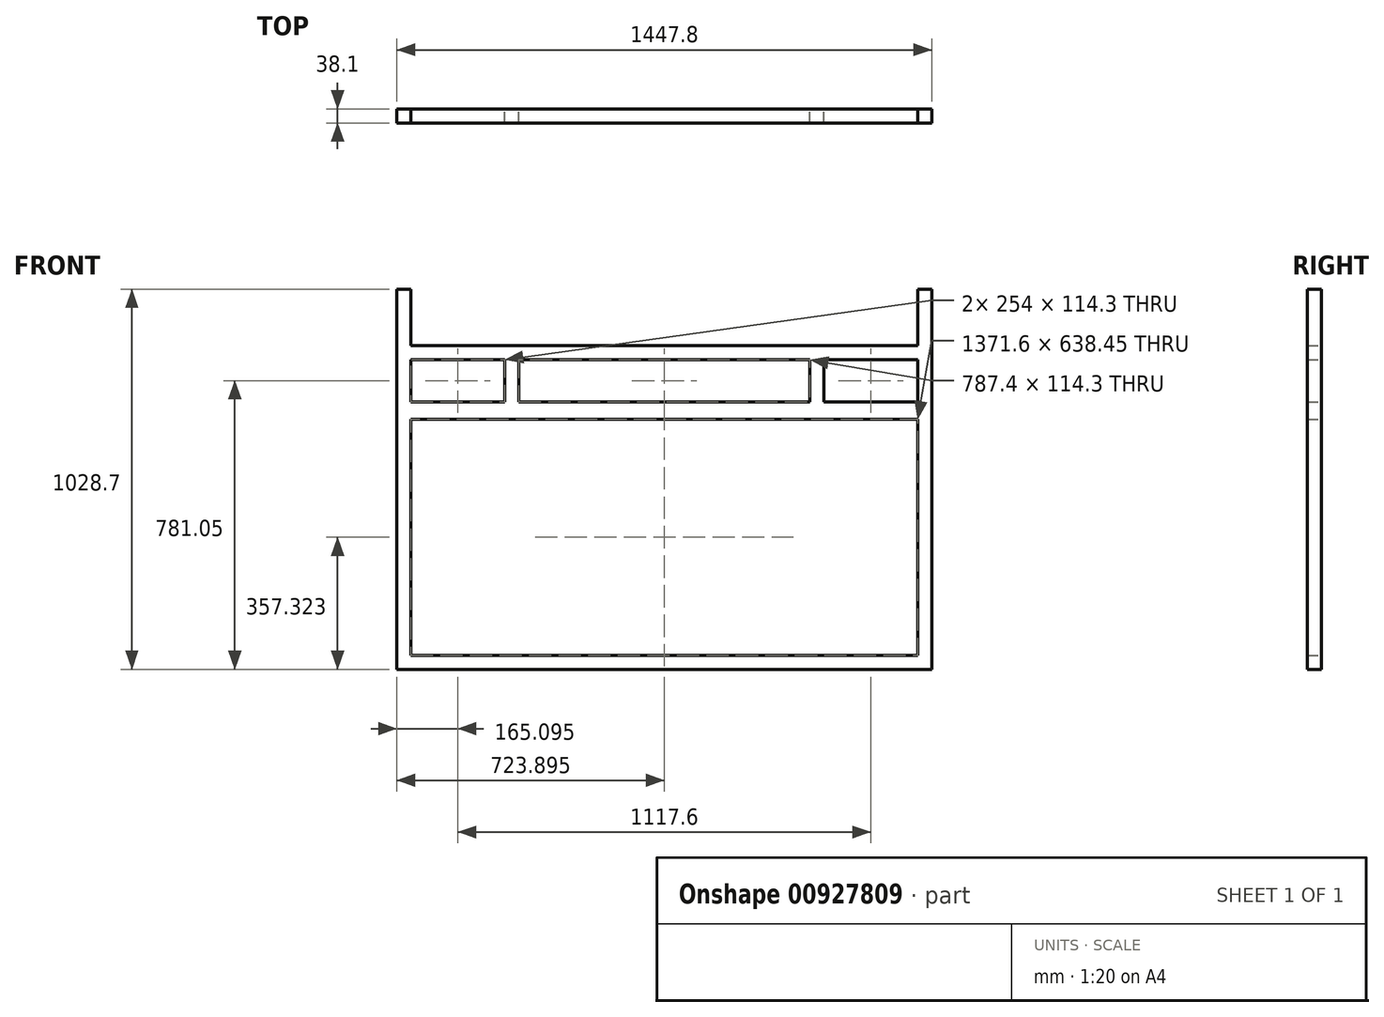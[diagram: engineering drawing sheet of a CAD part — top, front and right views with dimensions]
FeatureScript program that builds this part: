
annotation { "Feature Type Name" : "Feature", "Feature Type Description" : "" }
export const myFeature = defineFeature(function(context is Context, id is Id, definition is map)
    precondition{}
    {
        {
            var Q0;
            Q0=qCreatedBy(makeId("Front.planeOp"),FACE);
            var sketch = newSketch(context, id + "F0", { "sketchPlane" : qUnion([Q0])});
            skLineSegment(sketch, "E0.bottom", {"start": v(-457.01, 0) * mm, "end": v(990.79, 0) * mm});
            skLineSegment(sketch, "E0.top", {"start": v(-457.01, 38.1) * mm, "end": v(990.79, 38.1) * mm});
            skLineSegment(sketch, "E0.left", {"start": v(-457.01, 0) * mm, "end": v(-457.01, 38.1) * mm});
            skLineSegment(sketch, "E0.right", {"start": v(990.79, 0) * mm, "end": v(990.79, 38.1) * mm});
            skLineSegment(sketch, "E1", {"start": v(-457.01, 38.1) * mm, "end": v(-457.01, 723.9) * mm});
            skLineSegment(sketch, "E2.bottom", {"start": v(-457.01, 38.1) * mm, "end": v(-418.91, 38.1) * mm});
            skLineSegment(sketch, "E2.top", {"start": v(-457.01, 723.9) * mm, "end": v(-418.91, 723.9) * mm});
            skLineSegment(sketch, "E2.right", {"start": v(-418.91, 38.1) * mm, "end": v(-418.91, 723.9) * mm});
            skLineSegment(sketch, "E3.bottom", {"start": v(990.79, 38.1) * mm, "end": v(952.69, 38.1) * mm});
            skLineSegment(sketch, "E3.top", {"start": v(990.79, 723.9) * mm, "end": v(952.69, 723.9) * mm});
            skLineSegment(sketch, "E3.left", {"start": v(990.79, 38.1) * mm, "end": v(990.79, 723.9) * mm});
            skLineSegment(sketch, "E3.right", {"start": v(952.69, 38.1) * mm, "end": v(952.69, 723.9) * mm});
            skLineSegment(sketch, "E4.bottom", {"start": v(-418.91, 723.9) * mm, "end": v(952.69, 723.9) * mm});
            skLineSegment(sketch, "E4.top", {"start": v(-418.91, 676.55) * mm, "end": v(952.69, 676.55) * mm});
            skLineSegment(sketch, "E4.left", {"start": v(-418.91, 723.9) * mm, "end": v(-418.91, 676.55) * mm});
            skLineSegment(sketch, "E4.right", {"start": v(952.69, 723.9) * mm, "end": v(952.69, 676.55) * mm});
            skLineSegment(sketch, "E5.top", {"start": v(-457.01, 1028.7) * mm, "end": v(-418.91, 1028.7) * mm});
            skLineSegment(sketch, "E5.left", {"start": v(-457.01, 723.9) * mm, "end": v(-457.01, 1028.7) * mm});
            skLineSegment(sketch, "E5.right", {"start": v(-418.91, 723.9) * mm, "end": v(-418.91, 1028.7) * mm});
            skLineSegment(sketch, "E6.top", {"start": v(990.79, 1028.7) * mm, "end": v(952.69, 1028.7) * mm});
            skLineSegment(sketch, "E6.left", {"start": v(990.79, 723.9) * mm, "end": v(990.79, 1028.7) * mm});
            skLineSegment(sketch, "E6.right", {"start": v(952.69, 723.9) * mm, "end": v(952.69, 1028.7) * mm});
            skLineSegment(sketch, "E7.bottom", {"start": v(-418.91, 876.3) * mm, "end": v(952.69, 876.3) * mm});
            skLineSegment(sketch, "E7.top", {"start": v(-418.91, 838.2) * mm, "end": v(952.69, 838.2) * mm});
            skLineSegment(sketch, "E7.left", {"start": v(-418.91, 876.3) * mm, "end": v(-418.91, 838.2) * mm});
            skLineSegment(sketch, "E7.right", {"start": v(952.69, 876.3) * mm, "end": v(952.69, 838.2) * mm});
            skLineSegment(sketch, "E8.bottom", {"start": v(-164.91, 838.2) * mm, "end": v(-126.81, 838.2) * mm});
            skLineSegment(sketch, "E8.top", {"start": v(-164.91, 723.9) * mm, "end": v(-126.81, 723.9) * mm});
            skLineSegment(sketch, "E8.left", {"start": v(-164.91, 838.2) * mm, "end": v(-164.91, 723.9) * mm});
            skLineSegment(sketch, "E8.right", {"start": v(-126.81, 838.2) * mm, "end": v(-126.81, 723.9) * mm});
            skLineSegment(sketch, "E9.bottom", {"start": v(660.59, 838.2) * mm, "end": v(698.69, 838.2) * mm});
            skLineSegment(sketch, "E9.top", {"start": v(660.59, 723.9) * mm, "end": v(698.69, 723.9) * mm});
            skLineSegment(sketch, "E9.left", {"start": v(660.59, 838.2) * mm, "end": v(660.59, 723.9) * mm});
            skLineSegment(sketch, "E9.right", {"start": v(698.69, 838.2) * mm, "end": v(698.69, 723.9) * mm});
            skSolve(sketch);
        }
        {
            var Q0;
            {var subQ2=sQuery(id+"F0.wireOp",EDGE,"E7.bottom");var subQ4=sQuery(id+"F0.wireOp",EDGE,"E3.top");var subQ5=makeQuery(id+"F0.imprint","IMPRINT",EDGE,{"derivedFrom":subQ4});var subQ12=sQuery(id+"F0.wireOp",EDGE,"E2.top");var subQ13=makeQuery(id+"F0.imprint","IMPRINT",EDGE,{"derivedFrom":subQ12});var subQ14=sQuery(id+"F0.wireOp",EDGE,"E1");Q0=qUnion([makeQuery(id+"F0.imprint","IMPRINT",FACE,{"disambiguationData":[TD([[makeQuery(id+"F0.imprint","IMPRINT",EDGE,{"derivedFrom":sQuery(id+"F0.wireOp",EDGE,"E0.bottom")}),1.0]])]}),makeQuery(id+"F0.imprint","IMPRINT",FACE,{"disambiguationData":[TD([[subQ5,1.0]])]}),makeQuery(id+"F0.imprint","IMPRINT",FACE,{"disambiguationData":[TD([[makeQuery(id+"F0.imprint","IMPRINT",EDGE,{"derivedFrom":subQ2}),-1.0]])]}),makeQuery(id+"F0.imprint","IMPRINT",FACE,{"disambiguationData":[TD([[subQ13,1.0]])]}),makeQuery(id+"F0.imprint","IMPRINT",FACE,{"disambiguationData":[TD([[makeQuery(id+"F0.imprint","IMPRINT",EDGE,{"derivedFrom":subQ14}),-1.0]])]}),makeQuery(id+"F0.imprint","IMPRINT",FACE,{"disambiguationData":[TD([[subQ5,-1.0]])]})]);}
            var Q1;
            {var subQ2=sQuery(id+"F0.wireOp",EDGE,"E8.left");Q1=makeQuery(id+"F0.imprint","IMPRINT",FACE,{"disambiguationData":[TD([[makeQuery(id+"F0.imprint","IMPRINT",EDGE,{"derivedFrom":subQ2}),1.0]])]});}
            var Q2;
            {var subQ4=sQuery(id+"F0.wireOp",EDGE,"E4.top");Q2=makeQuery(id+"F0.imprint","IMPRINT",FACE,{"disambiguationData":[TD([[makeQuery(id+"F0.imprint","IMPRINT",EDGE,{"derivedFrom":subQ4}),1.0]])]});}
            var Q3;
            {var subQ0=sQuery(id+"F0.wireOp",EDGE,"E9.left");Q3=makeQuery(id+"F0.imprint","IMPRINT",FACE,{"disambiguationData":[TD([[makeQuery(id+"F0.imprint","IMPRINT",EDGE,{"derivedFrom":subQ0}),1.0]])]});}
            extrude(context, id + "F1", {"entities" : qUnion([Q0, Q1, Q2, Q3]), "depth" : 38.1 * mm, "offsetDistance" : 25.4 * mm});
        }
    });
